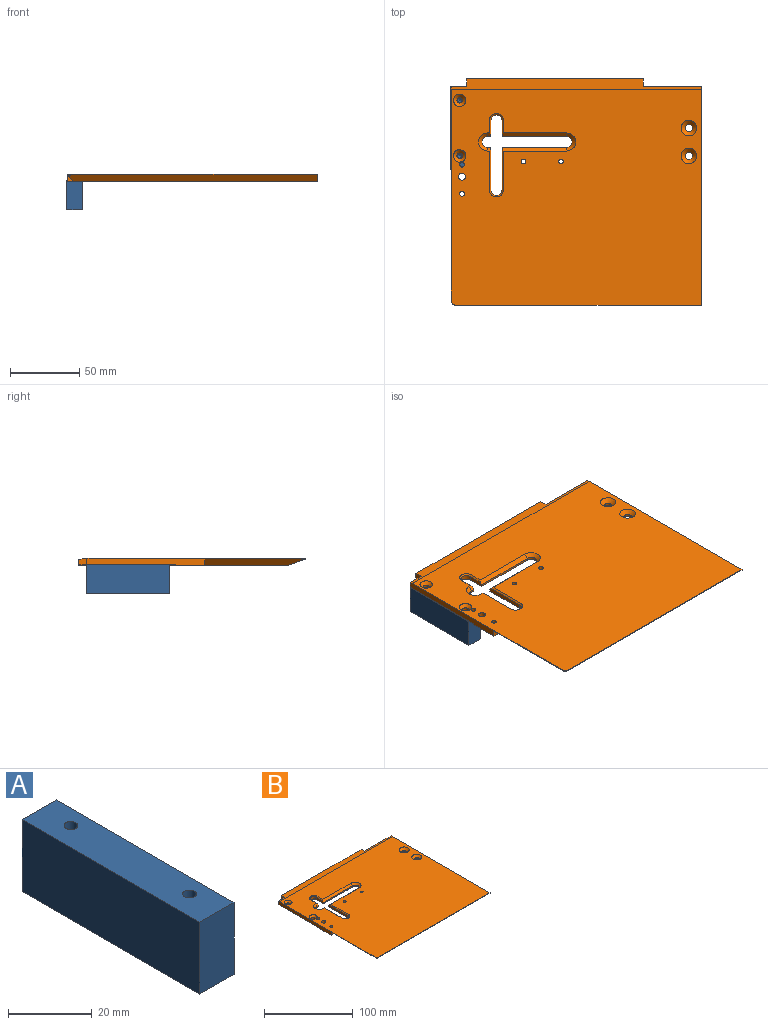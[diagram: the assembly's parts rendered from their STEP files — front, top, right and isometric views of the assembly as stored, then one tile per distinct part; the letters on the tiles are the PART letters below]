
ASSEMBLY  parts=2 mates=1
PART A: 14 faces, bbox 11.5x60x21 mm
  f0: plane 60x21mm, normal (-1,0,0), area 1260mm2, adj f1,f3,f4,f5
  f1: plane 21x11.5mm, normal (0,-1,0), area 241.5mm2, adj f0,f2,f4,f5
  f2: plane 60x21mm, normal (1,0,0), area 1260mm2, adj f1,f3,f4,f5
  f3: plane 21x11.5mm, normal (0,1,0), area 241.5mm2, adj f0,f2,f4,f5
  f4: plane 60x11.5mm, normal (0,0,1), area 672.9mm2, adj f0,f1,f2,f3,f11,f13
  f5: plane 60x11.5mm, normal (0,0,-1), area 650.7mm2, adj f0,f1,f2,f3,f7,f9
  f6: cone r=0mm half-angle=59deg, axis (0,0,-1), area 22.9mm2, adj f7
  f7: cylinder r=2.5mm len=18mm, axis (0,0,-1), area 282.7mm2, adj f5,f6
  f8: cone r=0mm half-angle=59deg, axis (0,0,-1), area 22.9mm2, adj f9
  f9: cylinder r=2.5mm len=18mm, axis (0,0,-1), area 282.7mm2, adj f5,f8
  f10: cone r=0mm half-angle=59deg, axis (0,0,1), area 10mm2, adj f11
  f11: cylinder r=1.65mm len=14.1mm, axis (0,0,1), area 146.2mm2, adj f4,f10
  f12: cone r=0mm half-angle=59deg, axis (0,0,1), area 10mm2, adj f13
  f13: cylinder r=1.65mm len=14.1mm, axis (0,0,1), area 146.2mm2, adj f4,f12
PART B: 72 faces, bbox 180x163x5 mm
  f0: plane 127x4.34mm, normal (0,1,0), area 551.2mm2, adj f1,f3,f26,f36,f64,f65
  f1: plane 180x150.64mm, normal (0,0,-1), area 23212mm2, adj f0,f2,f6,f11,f23,f25,f26,f29
  f2: plane 42x4.83mm, normal (0,1,0), area 192.7mm2, adj f1,f25,f26,f36,f67,f68
  f3: plane 5.5x4.33mm, normal (-1,0,0), area 22.5mm2, adj f0,f4,f36,f65
  f4: plane 11x4.33mm, normal (0,1,0), area 47.6mm2, adj f3,f23,f36,f65
  f5: cylinder r=1.65mm len=4.5mm, axis (0,0,1), area 46.7mm2, adj f28,f65
  f6: cylinder r=2.5mm len=5mm, axis (0,0,1), area 75.2mm2, adj f1,f28,f63,f65,f70
  f7: cylinder r=2.75mm len=5.5mm, axis (0,0,1), area 28.5mm2, adj f32,f68
  f8: cylinder r=2.75mm len=5.5mm, axis (0,0,1), area 28.5mm2, adj f33,f68
  f9: cylinder r=2.25mm len=4.5mm, axis (0,0,1), area 32.1mm2, adj f34,f65
  f10: cylinder r=2.25mm len=4.5mm, axis (0,0,1), area 32.1mm2, adj f35,f65
  f11: plane 179.51x12.36mm, normal (0,-0.34,-0.94), area 2337.3mm2, adj f1,f24,f25,f61,f71
  f12: plane 46.5x1.5mm, normal (0,1,0), area 69.8mm2, adj f13,f27,f39,f49
  f13: plane 30.5x3mm, normal (-1,0,0), area 90.4mm2, adj f12,f14,f39,f51,f57
  f14: cylinder r=4mm len=8mm, axis (0,0,1), area 37.7mm2, adj f13,f15,f53,f56
  f15: plane 30.5x3mm, normal (1,0,0), area 90.4mm2, adj f14,f16,f42,f54,f55
  f16: plane 2.5x1.5mm, normal (0,1,0), area 3.8mm2, adj f15,f17,f42,f52
  f17: cylinder r=4mm len=8mm, axis (0,0,1), area 18.8mm2, adj f16,f18,f41,f50
  f18: plane 2.5x1.5mm, normal (0,-1,0), area 3.8mm2, adj f17,f19,f40,f48
  f19: plane 11.5x3mm, normal (1,0,0), area 33.4mm2, adj f18,f20,f40,f46,f58
  f20: cylinder r=4mm len=8mm, axis (0,0,1), area 37.7mm2, adj f19,f21,f44,f59
  f21: plane 11.5x3mm, normal (-1,0,0), area 33.4mm2, adj f20,f22,f37,f43,f60
  f22: plane 46.5x1.5mm, normal (0,-1,0), area 69.8mm2, adj f21,f27,f37,f45
  f23: plane 154.5x5mm, normal (-1,0,0), area 427.4mm2, adj f1,f4,f28,f36,f61,f62,f63,f65
  f24: plane 177x0.5mm, normal (0,-1,0), area 88.5mm2, adj f11,f25,f28,f71
  f25: plane 157.5x5mm, normal (1,0,0), area 724.5mm2, adj f1,f2,f11,f24,f28,f36,f66,f68
  f26: plane 5.5x4.83mm, normal (1,0,0), area 25.2mm2, adj f0,f1,f2,f36
  f27: cylinder r=4mm len=8mm, axis (0,0,1), area 18.8mm2, adj f12,f22,f38,f47
  f28: plane 180x155.5mm, normal (0,0,1), area 26288.8mm2, adj f5,f6,f23,f24,f25,f29,f30,f31
  f29: cylinder r=1.65mm len=5mm, axis (0,0,1), area 51.8mm2, adj f1,f28
  f30: cylinder r=1.65mm len=5mm, axis (0,0,1), area 51.8mm2, adj f1,f28
  f31: cylinder r=1.65mm len=5mm, axis (0,0,1), area 51.8mm2, adj f1,f28
  f32: cone r=2.75mm half-angle=45deg, axis (0,0,1), area 105.7mm2, adj f7,f28
  f33: cone r=2.75mm half-angle=45deg, axis (0,0,1), area 105.7mm2, adj f8,f28
  f34: cone r=2.25mm half-angle=45deg, axis (0,0,1), area 66.7mm2, adj f9,f28
  f35: cone r=2.25mm half-angle=45deg, axis (0,0,1), area 66.7mm2, adj f10,f28
  f36: plane 180x7.5mm, normal (0,0.09,1), area 1062.5mm2, adj f0,f2,f3,f4,f23,f25,f26,f28
  f37: plane 46.5x2.5mm, normal (0,-0.71,0.71), area 163.7mm2, adj f21,f22,f28,f38,f60
  f38: cone r=6.5mm half-angle=45deg, axis (0,0,1), area 58.3mm2, adj f27,f28,f37,f39
  f39: plane 46.5x2.5mm, normal (0,0.71,0.71), area 163.7mm2, adj f12,f13,f28,f38,f57
  f40: plane 2.5x2.5mm, normal (0,-0.71,0.71), area 8.1mm2, adj f18,f19,f28,f41,f58
  f41: cone r=6.5mm half-angle=45deg, axis (0,0,1), area 58.3mm2, adj f17,f28,f40,f42
  f42: plane 2.5x2.5mm, normal (0,0.71,0.71), area 8.1mm2, adj f15,f16,f28,f41,f55
  f43: plane 11.5x1mm, normal (-0.71,0,-0.71), area 15.6mm2, adj f1,f21,f44,f45
  f44: cone r=4mm half-angle=45deg, axis (0,0,-1), area 20mm2, adj f1,f20,f43,f46
  f45: plane 46.5x1mm, normal (0,-0.71,-0.71), area 65.1mm2, adj f1,f22,f43,f47
  f46: plane 11.5x1mm, normal (0.71,0,-0.71), area 15.6mm2, adj f1,f19,f44,f48
  f47: cone r=4mm half-angle=45deg, axis (0,0,-1), area 20mm2, adj f1,f27,f45,f49
  f48: plane 2.5x1mm, normal (0,-0.71,-0.71), area 2.8mm2, adj f1,f18,f46,f50
  f49: plane 46.5x1mm, normal (0,0.71,-0.71), area 65.1mm2, adj f1,f12,f47,f51
  f50: cone r=4mm half-angle=45deg, axis (0,0,-1), area 20mm2, adj f1,f17,f48,f52
  f51: plane 30.5x1mm, normal (-0.71,0,-0.71), area 42.4mm2, adj f1,f13,f49,f53
  f52: plane 2.5x1mm, normal (0,0.71,-0.71), area 2.8mm2, adj f1,f16,f50,f54
  f53: cone r=4mm half-angle=45deg, axis (0,0,-1), area 20mm2, adj f1,f14,f51,f54
  f54: plane 30.5x1mm, normal (0.71,0,-0.71), area 42.4mm2, adj f1,f15,f52,f53
  f55: plane 29x1mm, normal (0.71,0,0.71), area 40.3mm2, adj f15,f28,f42,f56
  f56: cone r=5mm half-angle=45deg, axis (0,0,1), area 20mm2, adj f14,f28,f55,f57
  f57: plane 29x1mm, normal (-0.71,0,0.71), area 40.3mm2, adj f13,f28,f39,f56
  f58: plane 10x1mm, normal (0.71,0,0.71), area 13.4mm2, adj f19,f28,f40,f59
  f59: cone r=5mm half-angle=45deg, axis (0,0,1), area 20mm2, adj f20,f28,f58,f60
  f60: plane 10x1mm, normal (-0.71,0,0.71), area 13.4mm2, adj f21,f28,f37,f59
  f61: plane 71.15x4.5mm, normal (-0.71,0,-0.71), area 421.2mm2, adj f1,f11,f23,f62,f71
  f62: plane 4.5x4.5mm, normal (0,-1,0), area 10.1mm2, adj f1,f23,f61
  f63: plane 5.27x0.5mm, normal (0,1,0), area 2.6mm2, adj f1,f6,f23,f65
  f64: plane 67.12x0.5mm, normal (-1,0,0), area 33.6mm2, adj f0,f1,f65,f70
  f65: plane 69.9x12mm, normal (0,0,-1), area 729.7mm2, adj f0,f3,f4,f5,f6,f9,f10,f23
  f66: plane 17x0.5mm, normal (0,1,0), area 8.5mm2, adj f1,f25,f68,f69
  f67: plane 67x0.5mm, normal (1,0,0), area 33.5mm2, adj f1,f2,f68,f69
  f68: plane 70x20mm, normal (0,0,-1), area 1350.6mm2, adj f2,f7,f8,f25,f66,f67,f69
  f69: cylinder r=3mm len=3mm, axis (0,0,-1), area 2.4mm2, adj f1,f66,f67,f68
  f70: cylinder r=3mm len=2.78mm, axis (0,0,1), area 1.8mm2, adj f1,f6,f64,f65
  f71: cylinder r=3mm len=3mm, axis (0,0,-1), area 3.1mm2, adj f11,f23,f24,f28,f61
PLACE A at identity fixed
PLACE B t=(0.5,-97.5,25.5)mm
MATE fastened B.f10 <-> A.f12  axis (0,0,-1) through (6.5,10,21)mm
